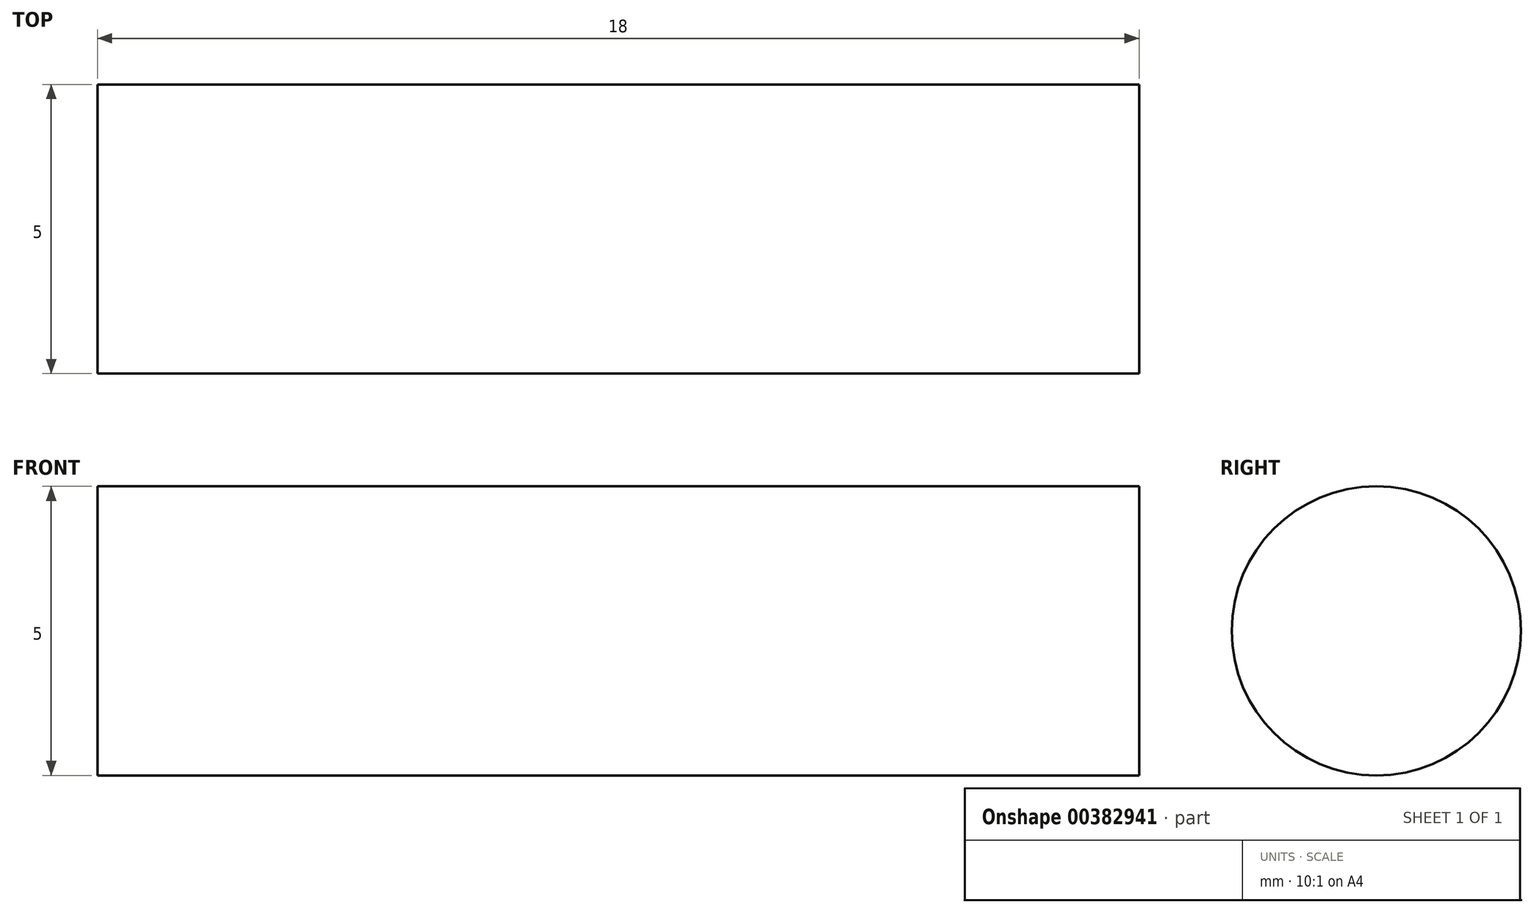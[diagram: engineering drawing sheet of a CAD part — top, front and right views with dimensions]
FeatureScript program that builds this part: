
annotation { "Feature Type Name" : "Feature", "Feature Type Description" : "" }
export const myFeature = defineFeature(function(context is Context, id is Id, definition is map)
    precondition{}
    {
        {
            var Q0;
            Q0=qCreatedBy(makeId("Right.planeOp"),FACE);
            var sketch = newSketch(context, id + "F0", { "sketchPlane" : qUnion([Q0])});
            skCircle(sketch, "E0", {"center": v(0, 0) * mm, "radius": 2.5 * mm});
            skSolve(sketch);
        }
        {
            var Q0;
            Q0 = qSketchRegion(id + "F0", true);
            extrude(context, id + "F1", {"entities" : qUnion([Q0]), "depth" : 18 * mm});
        }
    });
